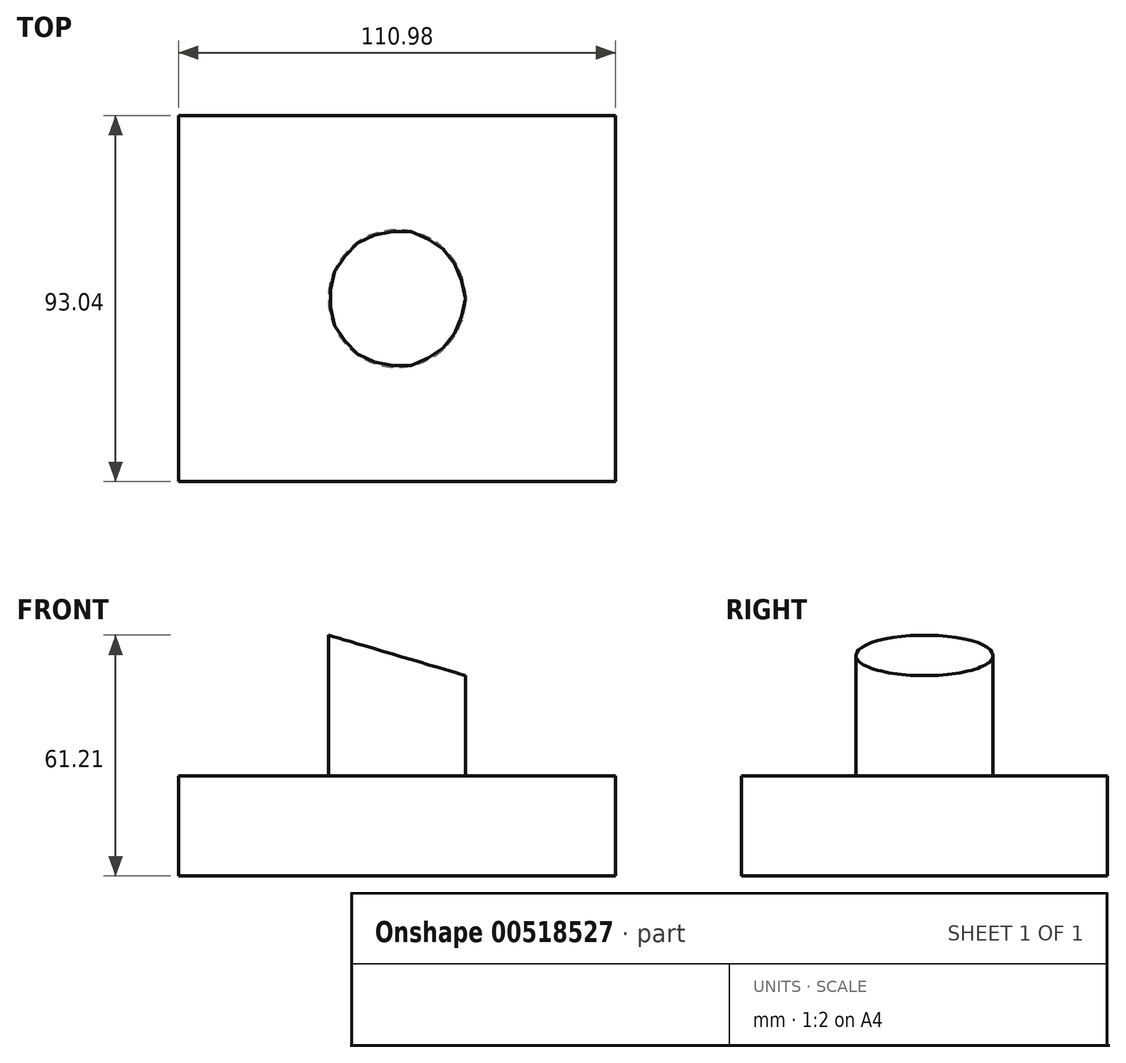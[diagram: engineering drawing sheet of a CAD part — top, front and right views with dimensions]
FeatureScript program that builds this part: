
annotation { "Feature Type Name" : "Feature", "Feature Type Description" : "" }
export const myFeature = defineFeature(function(context is Context, id is Id, definition is map)
    precondition{}
    {
        {
            var Q0;
            Q0=qCreatedBy(makeId("Top.planeOp"),FACE);
            var sketch = newSketch(context, id + "F0", { "sketchPlane" : qUnion([Q0])});
            skLineSegment(sketch, "E0.bottom", {"start": v(55.49, -46.52) * mm, "end": v(-55.49, -46.52) * mm});
            skLineSegment(sketch, "E0.top", {"start": v(55.49, 46.52) * mm, "end": v(-55.49, 46.52) * mm});
            skLineSegment(sketch, "E0.left", {"start": v(55.49, -46.52) * mm, "end": v(55.49, 46.52) * mm});
            skLineSegment(sketch, "E0.right", {"start": v(-55.49, -46.52) * mm, "end": v(-55.49, 46.52) * mm});
            skPoint(sketch, "E0.middle", {"position": v(0, 0) * mm});
            skSolve(sketch);
        }
        {
            var Q0;
            Q0 = qSketchRegion(id + "F0", true);
            extrude(context, id + "F1", {"entities" : qUnion([Q0]), "depth" : 25.4 * mm, "offsetDistance" : 25.4 * mm});
        }
        {
            var Q0;
            Q0=makeQuery(id+"F1.opExtrude","CAP_FACE",FACE,{"disambiguationData":[OSD([sQuery(id+"F0.wireOp",EDGE,"E0.bottom"),sQuery(id+"F0.wireOp",EDGE,"E0.top"),sQuery(id+"F0.wireOp",EDGE,"E0.left"),sQuery(id+"F0.wireOp",EDGE,"E0.right")])],"isStart":false});
            var sketch = newSketch(context, id + "F2", { "sketchPlane" : qUnion([Q0])});
            skCircle(sketch, "E1", {"center": v(0, 0) * mm, "radius": 17.44 * mm});
            skSolve(sketch);
        }
        {
            var Q0;
            Q0 = qSketchRegion(id + "F2", true);
            extrude(context, id + "F3", {"entities" : qUnion([Q0]), "operationType" : NewBodyOperationType.ADD, "depth" : 50.8 * mm, "offsetDistance" : 25.4 * mm});
        }
        {
            var Q0;
            Q0=qCreatedBy(makeId("Front.planeOp"),FACE);
            cPlane(context, id + "F4", {"entities" : qUnion([Q0]), "cplaneType" : CPlaneType.OFFSET, "offset" : 25.4 * mm, "width" : 152.4 * mm, "height" : 152.4 * mm});
        }
        {
            var Q0;
            Q0=qCreatedBy(id+"F4.planeOp",FACE);
            var sketch = newSketch(context, id + "F5", { "sketchPlane" : qUnion([Q0])});
            skLineSegment(sketch, "E2", {"start": v(-29.68, 64.82) * mm, "end": v(34.03, 46.02) * mm});
            skLineSegment(sketch, "E3", {"start": v(34.03, 79.69) * mm, "end": v(-31.5, 79.69) * mm});
            skLineSegment(sketch, "E4", {"start": v(-31.5, 79.69) * mm, "end": v(-29.68, 64.82) * mm});
            skLineSegment(sketch, "E5", {"start": v(34.03, 79.69) * mm, "end": v(34.03, 46.02) * mm});
            skSolve(sketch);
        }
        {
            var Q0;
            Q0 = qSketchRegion(id + "F5", true);
            extrude(context, id + "F6", {"entities" : qUnion([Q0]), "operationType" : NewBodyOperationType.REMOVE, "oppositeDirection" : true, "depth" : 58.93 * mm, "offsetDistance" : 25.4 * mm});
        }
    });
